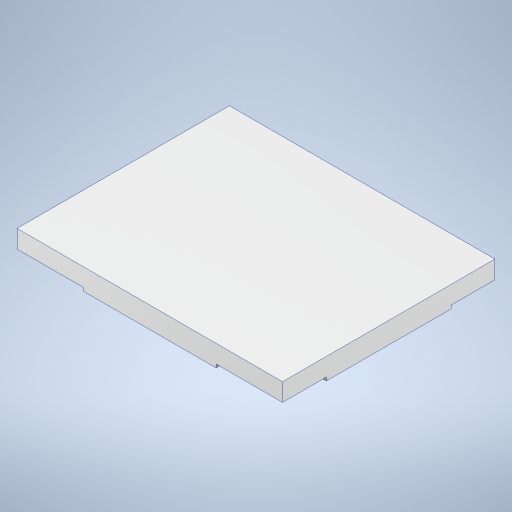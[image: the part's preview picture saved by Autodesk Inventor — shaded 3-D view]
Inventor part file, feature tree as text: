
AUTODESK INVENTOR PART (.ipt)
format: ipt  version: 2024 (Build 280153000, 153)  size: 303,104 bytes
history: native  units: mm
features: extrude x6, sketch x6, fillet x2, projected_geometry x1
ambient origin geometry x8: Origin, YZ Plane, XZ Plane, XY Plane, X Axis, Y Axis, Z Axis, Center Point
bodies: Solid1 (feature_tree)
feature tree (15):
  extrude  "Extrusion1"  Depth=200.0mm
  extrude  "Extrusion2"  Depth=60.0mm
  extrude  "Extrusion3"  Depth=12.0mm
  extrude  "Extrusion6"  Depth=5.0mm TaperAngle=0.0deg
  fillet  "Fillet1"  Radius=12.0mm
  fillet  "Fillet2"  Radius=25.0mm
  extrude  "Extrusion7"  Depth=50.0mm
  extrude  "Extrusion8"  Depth=50.0mm
  sketch  "Sketch1"  dims[d0=160.0mm d1=200.0mm]
  sketch  "Sketch2"  dims[d2=11.0mm d3=0.0mm d4=60.0mm]
  sketch  "Sketch3"  dims[d5=60.0mm d6=12.0mm]
  projected_geometry  "Projected Loop1"
  sketch  "Sketch7"  dims[d7=10.0mm d8=0.0mm d9=5.0mm d10=0.0mm d17=12.0mm d18=25.0mm]
  sketch  "Sketch8"  dims[d19=25.0mm d20=50.0mm]
  sketch  "Sketch10"  dims[d21=50.0mm d22=50.0mm d23=50.0mm d24=10.0mm d25=0.0mm d26=4.0mm d27=10.0mm d28=1000.0mm d29=0.0mm d30=50.0mm d31=50.0mm d32=50.0mm d33=50.0mm d34=33.0mm d35=33.0mm d36=0.0mm d37=2.5mm d38=0.0mm]
